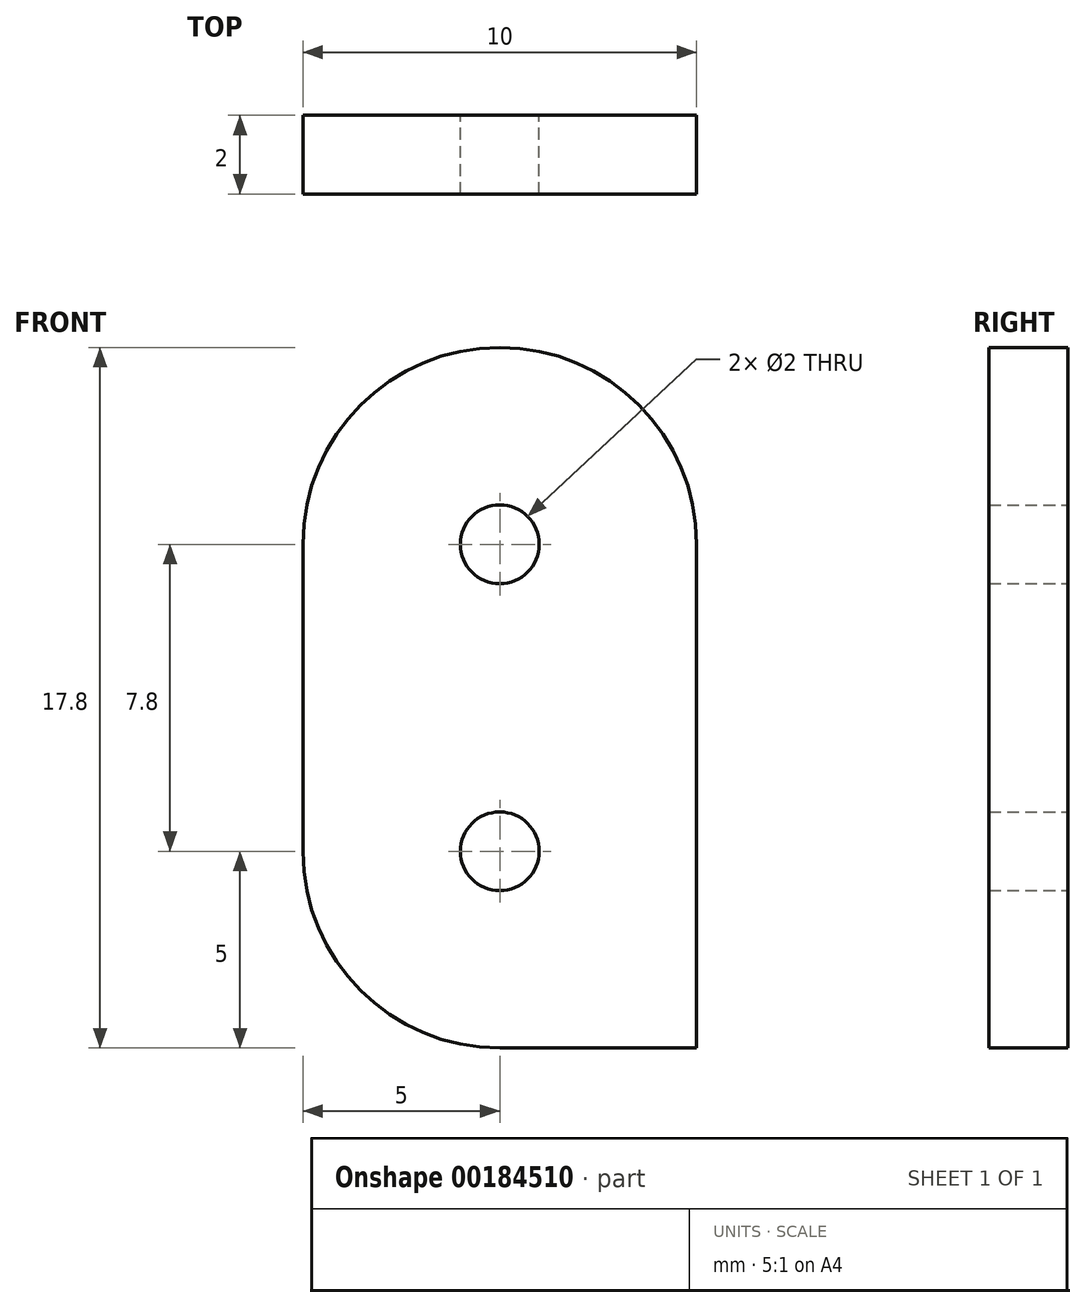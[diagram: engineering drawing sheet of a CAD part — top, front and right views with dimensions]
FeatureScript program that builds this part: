
annotation { "Feature Type Name" : "Feature", "Feature Type Description" : "" }
export const myFeature = defineFeature(function(context is Context, id is Id, definition is map)
    precondition{}
    {
        {
            var Q0;
            Q0=qCreatedBy(makeId("Front.planeOp"),FACE);
            var sketch = newSketch(context, id + "F0", { "sketchPlane" : qUnion([Q0])});
            skLineSegment(sketch, "E0.bottom", {"start": v(0, 0) * mm, "end": v(10, 0) * mm});
            skLineSegment(sketch, "E0.top", {"start": v(0, 17.8) * mm, "end": v(10, 17.8) * mm});
            skLineSegment(sketch, "E0.left", {"start": v(0, 0) * mm, "end": v(0, 17.8) * mm});
            skLineSegment(sketch, "E0.right", {"start": v(10, 0) * mm, "end": v(10, 17.8) * mm});
            skCircle(sketch, "E1", {"center": v(5, 12.8) * mm, "radius": 1 * mm});
            skCircle(sketch, "E2", {"center": v(5, 5) * mm, "radius": 1 * mm});
            skSolve(sketch);
        }
        {
            var Q0;
            Q0 = qSketchRegion(id + "F0", true);
            extrude(context, id + "F1", {"entities" : qUnion([Q0]), "depth" : 2 * mm});
        }
        {
            var Q0;
            Q0=makeQuery(id+"F1.opExtrude","SWEPT_EDGE",EDGE,{"disambiguationData":[OSD([sQuery(id+"F0.wireOp",EDGE,"E0.top"),sQuery(id+"F0.wireOp",EDGE,"E0.left")])]});
            var Q1;
            Q1=makeQuery(id+"F1.opExtrude","SWEPT_EDGE",EDGE,{"disambiguationData":[OSD([sQuery(id+"F0.wireOp",EDGE,"E0.top"),sQuery(id+"F0.wireOp",EDGE,"E0.right")])]});
            var Q2;
            Q2=makeQuery(id+"F1.opExtrude","SWEPT_EDGE",EDGE,{"disambiguationData":[OSD([sQuery(id+"F0.wireOp",EDGE,"E0.bottom"),sQuery(id+"F0.wireOp",EDGE,"E0.left")])]});
            fillet(context, id + "F2", {"entities" : qUnion([Q0, Q1, Q2]), "radius" : 5 * mm, "tangentPropagation" : true, "allowEdgeOverflow" : false});
        }
    });
